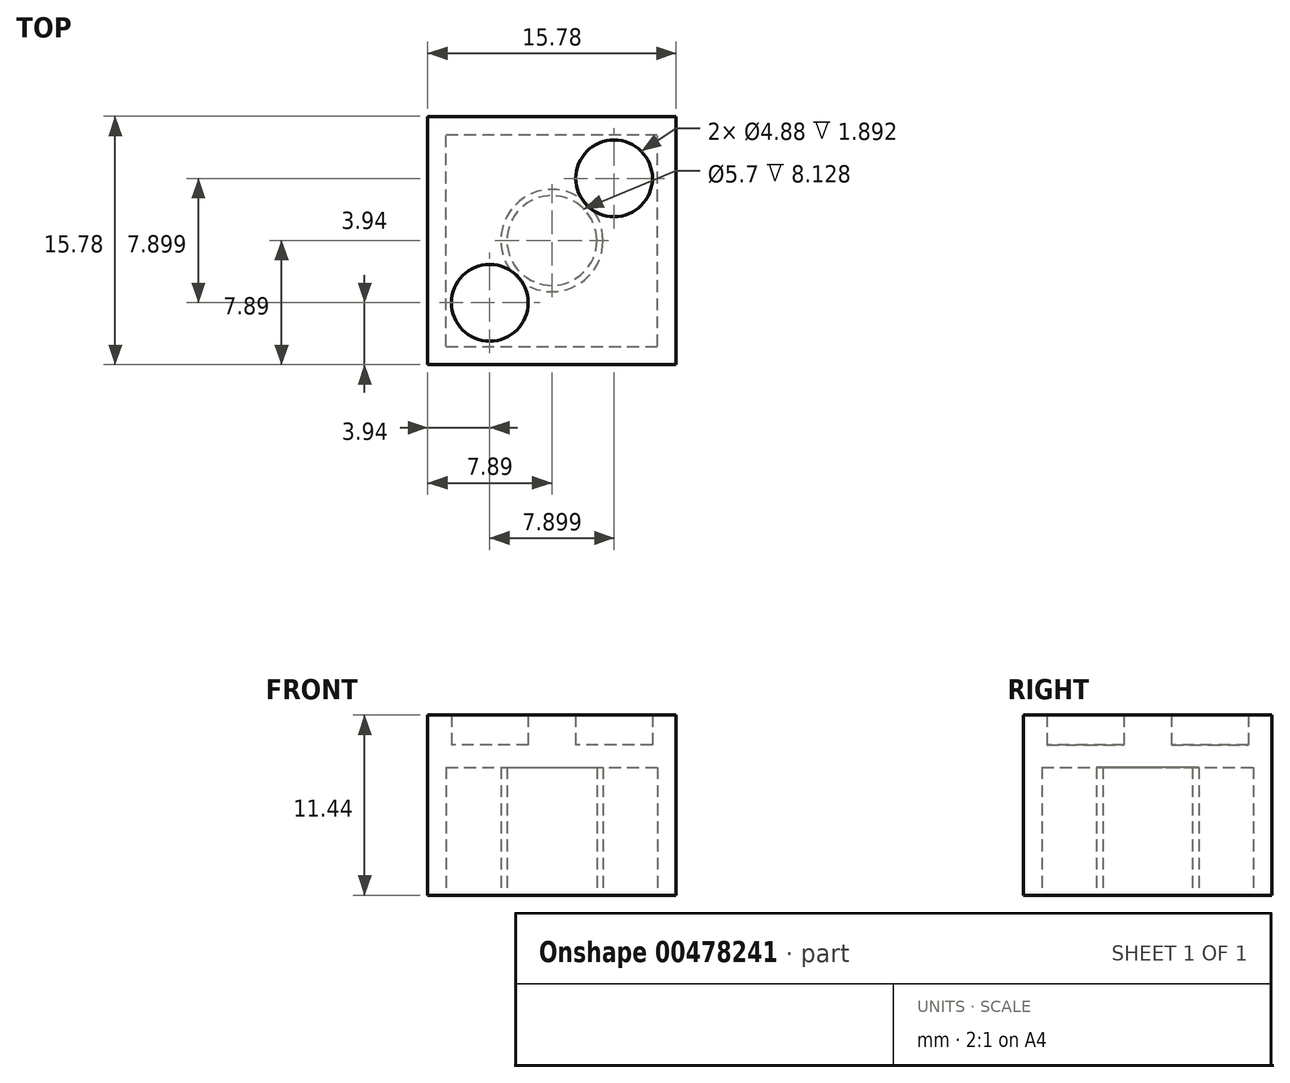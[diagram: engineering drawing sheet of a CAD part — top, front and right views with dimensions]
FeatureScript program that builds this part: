
annotation { "Feature Type Name" : "Feature", "Feature Type Description" : "" }
export const myFeature = defineFeature(function(context is Context, id is Id, definition is map)
    precondition{}
    {
        {
            var Q0;
            Q0=qCreatedBy(makeId("Top.planeOp"),FACE);
            var sketch = newSketch(context, id + "F0", { "sketchPlane" : qUnion([Q0])});
            skLineSegment(sketch, "E0.bottom", {"start": v(-7.89, 7.89) * mm, "end": v(7.89, 7.89) * mm});
            skLineSegment(sketch, "E0.top", {"start": v(-7.89, -7.89) * mm, "end": v(7.89, -7.89) * mm});
            skLineSegment(sketch, "E0.left", {"start": v(-7.89, 7.89) * mm, "end": v(-7.89, -7.89) * mm});
            skLineSegment(sketch, "E0.right", {"start": v(7.89, 7.89) * mm, "end": v(7.89, -7.89) * mm});
            skPoint(sketch, "E0.middle", {"position": v(0, 0) * mm});
            skSolve(sketch);
        }
        {
            var Q0;
            Q0=makeQuery(id+"F0.imprint","IMPRINT",FACE,{"disambiguationData":[TD([[makeQuery(id+"F0.imprint","IMPRINT",EDGE,{"derivedFrom":sQuery(id+"F0.wireOp",EDGE,"E0.bottom")}),-1.0]])]});
            extrude(context, id + "F1", {"entities" : qUnion([Q0]), "depth" : 9.55 * mm});
        }
        {
            var Q0;
            Q0=makeQuery(id+"F1.opExtrude","CAP_FACE",FACE,{"disambiguationData":[OSD([sQuery(id+"F0.wireOp",EDGE,"E0.bottom"),sQuery(id+"F0.wireOp",EDGE,"E0.top"),sQuery(id+"F0.wireOp",EDGE,"E0.left"),sQuery(id+"F0.wireOp",EDGE,"E0.right")])],"isStart":false});
            var sketch = newSketch(context, id + "F2", { "sketchPlane" : qUnion([Q0])});
            skCircle(sketch, "E1", {"center": v(-3.95, 3.95) * mm, "radius": 2.44 * mm});
            skCircle(sketch, "E2.MirrorC", {"center": v(3.95, 3.95) * mm, "radius": 2.44 * mm});
            skCircle(sketch, "E3.MirrorC", {"center": v(-3.95, -3.95) * mm, "radius": 2.44 * mm});
            skCircle(sketch, "E4.MirrorC", {"center": v(3.95, -3.95) * mm, "radius": 2.44 * mm});
            skSolve(sketch);
        }
        {
            var Q0;
            Q0=makeQuery(id+"F2.imprint","IMPRINT",FACE,{"disambiguationData":[TD([[makeQuery(id+"F2.imprint","IMPRINT",EDGE,{"derivedFrom":sQuery(id+"F2.wireOp",EDGE,"E2.MirrorC")}),-1.0]])]});
            var Q1;
            Q1=makeQuery(id+"F2.imprint","IMPRINT",FACE,{"disambiguationData":[TD([[makeQuery(id+"F2.imprint","IMPRINT",EDGE,{"derivedFrom":sQuery(id+"F2.wireOp",EDGE,"E3.MirrorC")}),-1.0]])]});
            var Q2;
            Q2=makeQuery(id+"F2.imprint","IMPRINT",FACE,{"disambiguationData":[TD([[makeQuery(id+"F2.imprint","IMPRINT",EDGE,{"derivedFrom":sQuery(id+"F2.wireOp",EDGE,"E4.MirrorC")}),1.0]])]});
            var Q3;
            Q3=makeQuery(id+"F2.imprint","IMPRINT",FACE,{"disambiguationData":[TD([[makeQuery(id+"F2.imprint","IMPRINT",EDGE,{"derivedFrom":sQuery(id+"F2.wireOp",EDGE,"E1")}),1.0]])]});
            extrude(context, id + "F3", {"entities" : qUnion([Q0, Q1, Q2, Q3]), "operationType" : NewBodyOperationType.ADD, "depth" : 1.9 * mm});
        }
        {
            var Q0;
            Q0=makeQuery(id+"F1.opExtrude","CAP_FACE",FACE,{"disambiguationData":[OSD([sQuery(id+"F0.wireOp",EDGE,"E0.bottom"),sQuery(id+"F0.wireOp",EDGE,"E0.top"),sQuery(id+"F0.wireOp",EDGE,"E0.left"),sQuery(id+"F0.wireOp",EDGE,"E0.right")])],"isStart":true});
            var sketch = newSketch(context, id + "F4", { "sketchPlane" : qUnion([Q0])});
            skLineSegment(sketch, "E5.bottom", {"start": v(-6.72, 6.72) * mm, "end": v(6.72, 6.72) * mm});
            skLineSegment(sketch, "E5.top", {"start": v(-6.72, -6.72) * mm, "end": v(6.72, -6.72) * mm});
            skLineSegment(sketch, "E5.left", {"start": v(-6.72, 6.72) * mm, "end": v(-6.72, -6.72) * mm});
            skLineSegment(sketch, "E5.right", {"start": v(6.72, 6.72) * mm, "end": v(6.72, -6.72) * mm});
            skPoint(sketch, "E5.middle", {"position": v(0, 0) * mm});
            skSolve(sketch);
        }
        {
            var Q0;
            Q0=makeQuery(id+"F4.imprint","IMPRINT",FACE,{"disambiguationData":[TD([[makeQuery(id+"F4.imprint","IMPRINT",EDGE,{"derivedFrom":sQuery(id+"F4.wireOp",EDGE,"E5.bottom")}),-1.0]])]});
            extrude(context, id + "F5", {"entities" : qUnion([Q0]), "operationType" : NewBodyOperationType.REMOVE, "depth" : -1 * 8.13 * mm});
        }
        {
            var Q0;
            Q0=makeQuery(id+"F4.imprint","IMPRINT",FACE,{"disambiguationData":[TD([[makeQuery(id+"F4.imprint","IMPRINT",EDGE,{"derivedFrom":sQuery(id+"F4.wireOp",EDGE,"E5.bottom")}),-1.0]])]});
            var sketch = newSketch(context, id + "F6", { "sketchPlane" : qUnion([Q0])});
            skCircle(sketch, "E6", {"center": v(0, 0) * mm, "radius": 3.24 * mm});
            skCircle(sketch, "E7", {"center": v(0, 0) * mm, "radius": 2.85 * mm});
            skSolve(sketch);
        }
        {
            var Q0;
            Q0 = qSketchRegion(id + "F6", true);
            extrude(context, id + "F7", {"entities" : qUnion([Q0]), "depth" : -1 * 8.13 * mm});
        }
    });
